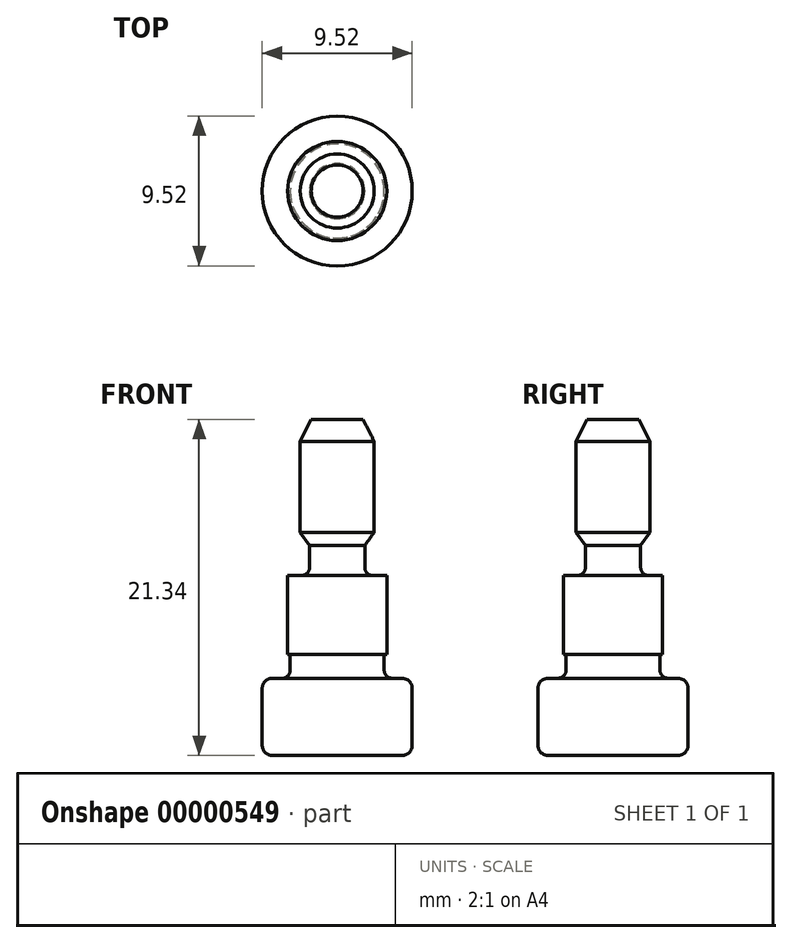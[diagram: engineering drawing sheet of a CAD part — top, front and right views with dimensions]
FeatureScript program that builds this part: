
annotation { "Feature Type Name" : "Feature", "Feature Type Description" : "" }
export const myFeature = defineFeature(function(context is Context, id is Id, definition is map)
    precondition{}
    {
        {
            var Q0;
            Q0 = qCreatedBy(makeId("Front.planeOp"), FACE);
            var sketch = newSketch(context, id + "F0", { "sketchPlane" : qUnion([Q0])});
            skLineSegment(sketch, "E0", {"start": v(0, 0) * mm, "end": v(4.76, 0) * mm});
            skLineSegment(sketch, "E1", {"start": v(4.76, 0) * mm, "end": v(4.76, 4.9) * mm});
            skLineSegment(sketch, "E2", {"start": v(4.76, 4.9) * mm, "end": v(2.98, 4.9) * mm});
            skLineSegment(sketch, "E3", {"start": v(2.98, 4.9) * mm, "end": v(2.98, 6.43) * mm});
            skLineSegment(sketch, "E4", {"start": v(2.98, 6.43) * mm, "end": v(3.15, 6.43) * mm});
            skLineSegment(sketch, "E5", {"start": v(3.15, 6.43) * mm, "end": v(3.15, 11.43) * mm});
            skLineSegment(sketch, "E6", {"start": v(3.15, 11.43) * mm, "end": v(1.75, 11.43) * mm});
            skLineSegment(sketch, "E7", {"start": v(1.75, 11.43) * mm, "end": v(1.75, 13.34) * mm});
            skLineSegment(sketch, "E8", {"start": v(1.75, 13.33) * mm, "end": v(2.35, 14.17) * mm});
            skLineSegment(sketch, "E9", {"start": v(2.35, 14.17) * mm, "end": v(2.35, 19.94) * mm});
            skLineSegment(sketch, "E10", {"start": v(2.35, 19.94) * mm, "end": v(1.65, 21.34) * mm});
            skLineSegment(sketch, "E11", {"start": v(1.65, 21.34) * mm, "end": v(0, 21.34) * mm});
            skLineSegment(sketch, "E12", {"start": v(0, 21.34) * mm, "end": v(0, 0) * mm});
            skSolve(sketch);
        }
        {
            var Q0;
            Q0=makeQuery(id+"F0.imprint","IMPRINT",FACE,{"disambiguationData":[TD([[makeQuery(id+"F0.imprint","IMPRINT",EDGE,{"derivedFrom":sQuery(id+"F0.wireOp",EDGE,"E0")}),1.0]])]});
            var Q1;
            Q1=sQuery(id+"F0.wireOp",EDGE,"E12");
            revolve(context, id + "F1", {"entities" : qUnion([Q0]), "axis" : qUnion([Q1]), "revolveType" : RevolveType.FULL});
        }
        {
            var Q0;
            Q0=makeQuery(id+"F1.opRevolve","SWEPT_EDGE",EDGE,{"disambiguationData":[OSD([sQuery(id+"F0.wireOp",EDGE,"E2"),sQuery(id+"F0.wireOp",EDGE,"E3")])]});
            var Q1;
            Q1=makeQuery(id+"F1.opRevolve","SWEPT_EDGE",EDGE,{"disambiguationData":[OSD([sQuery(id+"F0.wireOp",EDGE,"E6"),sQuery(id+"F0.wireOp",EDGE,"E7")])]});
            fillet(context, id + "F2", {"entities" : qUnion([Q0, Q1]), "radius" : 0.5 * mm, "tangentPropagation" : true, "allowEdgeOverflow" : false});
        }
        {
            var Q0;
            Q0=makeQuery(id+"F1.opRevolve","SWEPT_EDGE",EDGE,{"disambiguationData":[OSD([sQuery(id+"F0.wireOp",EDGE,"E0"),sQuery(id+"F0.wireOp",EDGE,"E1")])]});
            var Q1;
            Q1=makeQuery(id+"F1.opRevolve","SWEPT_EDGE",EDGE,{"disambiguationData":[OSD([sQuery(id+"F0.wireOp",EDGE,"E1"),sQuery(id+"F0.wireOp",EDGE,"E2")])]});
            fillet(context, id + "F3", {"entities" : qUnion([Q0, Q1]), "radius" : 0.64 * mm, "tangentPropagation" : true, "allowEdgeOverflow" : false});
        }
    });
